# Revit family: Midea_FCU_two pipe 2th Ceiling&Floor MKH3-700R3(R4)(DC50,60Hz)-Floor
name_source: partatom
category: Mechanical Equipment
revit_build: Autodesk Revit 2013 (Build: 20120221_2030(x64)
units: mm (PartAtom-declared; Revit-internal decimal feet)

## types (2) — shared parameters
Circuit breaker = 15 A
Condensation = water
Depth = 1360 mm  [stored 4.46194 ft]
Description = High efficiency water cooled
Drain pipe = 18.5 mm  [stored 0.0606955 ft]
Height = 200 mm  [stored 0.656168 ft]
Installation = Indoor installation
Liquid pipe = 19.05 mm  [stored 0.0625 ft]
Machine material = Galvanized Steel
Manufacturer = Midea
Panel color = -
Power supply = 220-240V ~50Hz/60Hz
Series = FCU
Width = 495 mm  [stored 1.62402 ft]
clearance access behind = 50 mm  [stored 0.164042 ft]
clearance access down = 90 mm  [stored 0.295276 ft]
clearance access left = 150 mm
clearance access right = 150 mm
clearance access up = 1500 mm  [stored 4.92126 ft]

## per-type parameters (varying)
| type | Air Flow(H/M/L) | Cooling Capacity(H/M/L) | Heating Capacity(H/M/L) | Net Weight | Power Input(H/M/L) | Rated current |
| MKH3-700-R3 | 1190/855/555 m3/h | 6.00/5.03/3.71 kW | 6.15/4.92/3.49 kW | 20.50 kg | 123/98/68 W | 1 A |
| MKH3-700-R4 | 1150/885/591 m3/h | 6.75/5.80/4.24 kW | 7.15/5.81/4.04 kW | 21.70 kg | 110/89/64 W | 0 A |

note: column(s) folded — value = type name in every type: Model

note: [stored X ft] marks values corroborated as IEEE doubles in the binary element streams (Revit-internal decimal feet)

## geometry (parser evidence)
native form markers: Blend x2, Sweep x3
no freeform markers — native parametric forms only
